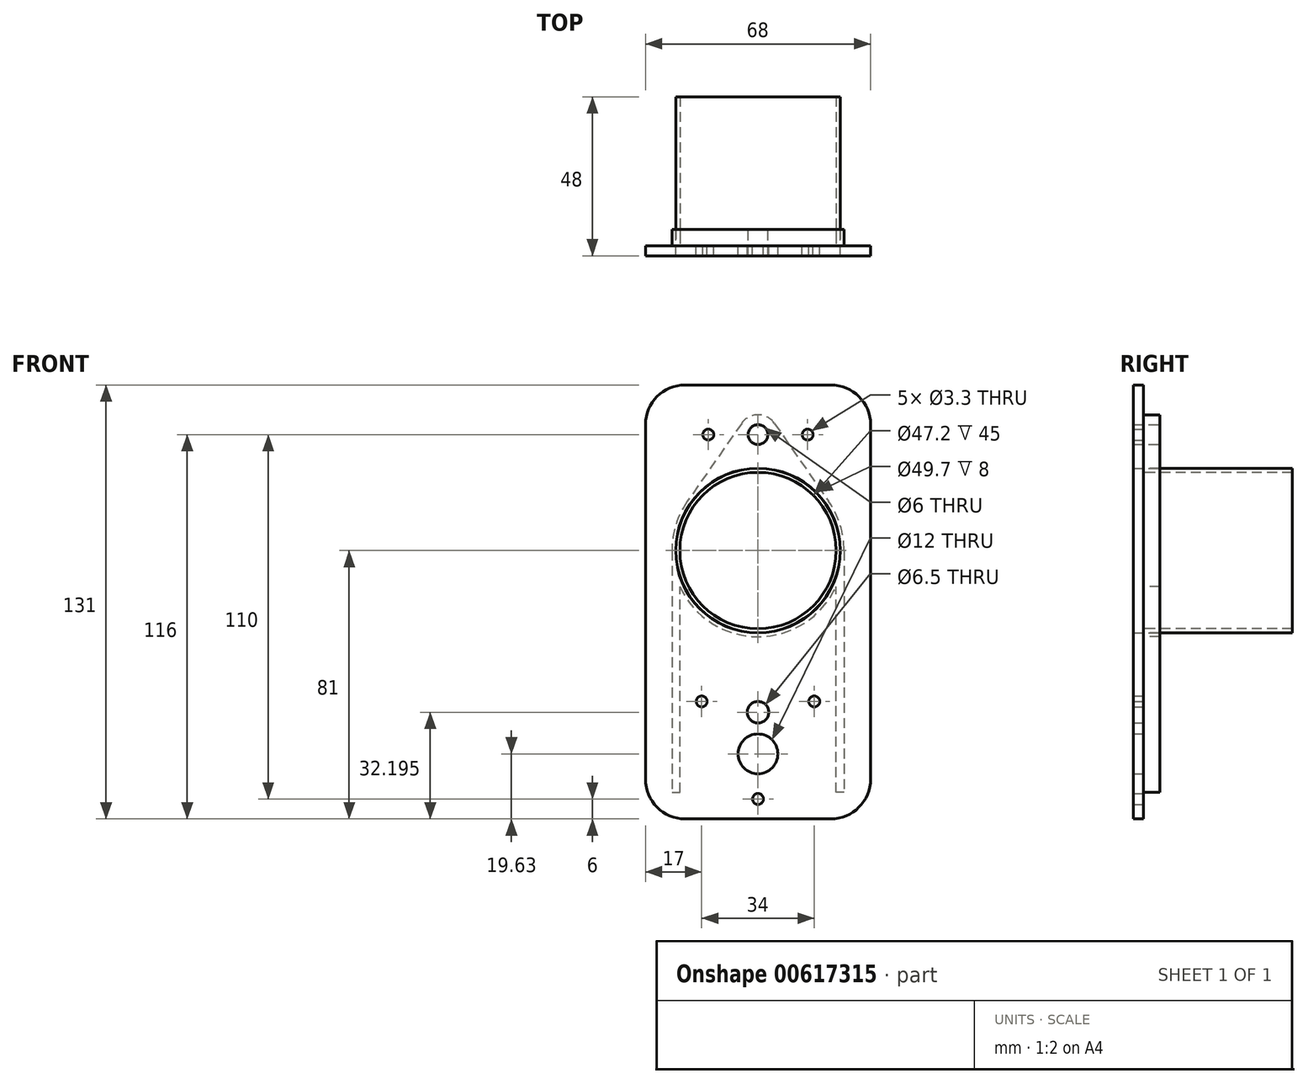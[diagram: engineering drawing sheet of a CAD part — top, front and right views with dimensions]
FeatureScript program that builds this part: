
annotation { "Feature Type Name" : "Feature", "Feature Type Description" : "" }
export const myFeature = defineFeature(function(context is Context, id is Id, definition is map)
    precondition{}
    {
        {
            var Q0;
            Q0=qCreatedBy(makeId("Front.planeOp"),FACE);
            var sketch = newSketch(context, id + "F0", { "sketchPlane" : qUnion([Q0])});
            skLineSegment(sketch, "E0.bottom", {"start": v(34, -65.5) * mm, "end": v(-34, -65.5) * mm});
            skLineSegment(sketch, "E0.top", {"start": v(34, 65.5) * mm, "end": v(-34, 65.5) * mm});
            skLineSegment(sketch, "E0.left", {"start": v(34, -65.5) * mm, "end": v(34, 65.5) * mm});
            skLineSegment(sketch, "E0.right", {"start": v(-34, -65.5) * mm, "end": v(-34, 65.5) * mm});
            skPoint(sketch, "E0.middle", {"position": v(0, 0) * mm});
            skCircle(sketch, "E1", {"center": v(0, 15.5) * mm, "radius": 24.85 * mm});
            skLineSegment(sketch, "E2", {"start": v(0, 15.5) * mm, "end": v(0, -65.5) * mm, "construction": true});
            skPoint(sketch, "E3", {"position": v(0, -59.5) * mm});
            skPoint(sketch, "E4", {"position": v(-17, -30.06) * mm});
            skPoint(sketch, "E5.MirrorP", {"position": v(17, -30.06) * mm});
            skLineSegment(sketch, "E6", {"start": v(-17, -30.06) * mm, "end": v(17, -30.06) * mm, "construction": true});
            skLineSegment(sketch, "E7", {"start": v(0, -59.5) * mm, "end": v(-17, -30.06) * mm, "construction": true});
            skLineSegment(sketch, "E8", {"start": v(17, -30.06) * mm, "end": v(-8.5, -44.78) * mm, "construction": true});
            skCircle(sketch, "E9", {"center": v(0, -39.87) * mm, "radius": 12 * mm, "construction": true});
            skCircle(sketch, "E10", {"center": v(0, 50.5) * mm, "radius": 3 * mm});
            skCircle(sketch, "E11", {"center": v(0, -45.87) * mm, "radius": 6 * mm});
            skCircle(sketch, "E12", {"center": v(0, -33.3) * mm, "radius": 3.25 * mm});
            skPoint(sketch, "E13", {"position": v(15, 50.5) * mm});
            skPoint(sketch, "E14.MirrorP", {"position": v(-15, 50.5) * mm});
            skSolve(sketch);
        }
        {
            var Q0;
            Q0 = qSketchRegion(id + "F0", true);
            extrude(context, id + "F1", {"entities" : qUnion([Q0]), "depth" : 3 * mm, "offsetDistance" : 25 * mm});
        }
        {
            var Q0;
            Q0=makeQuery(id+"F1.opExtrude","CAP_FACE",FACE,{"disambiguationData":[OSD([sQuery(id+"F0.wireOp",EDGE,"E0.bottom"),sQuery(id+"F0.wireOp",EDGE,"E0.top"),sQuery(id+"F0.wireOp",EDGE,"E0.left"),sQuery(id+"F0.wireOp",EDGE,"E0.right"),sQuery(id+"F0.wireOp",EDGE,"E1"),sQuery(id+"F0.wireOp",EDGE,"lBdVOncp-TCnz-bJnv-wLVM-4AzIkIplRtc7"),sQuery(id+"F0.wireOp",EDGE,"E10")])],"isStart":true});
            var sketch = newSketch(context, id + "F2", { "sketchPlane" : qUnion([Q0])});
            skCircle(sketch, "E15.0", {"center": v(0, 15.5) * mm, "radius": 24.85 * mm});
            skCircle(sketch, "E16.0", {"center": v(0, 50.5) * mm, "radius": 3 * mm});
            skArc(sketch, "E17", {"start": v(-23.6, 4.59) * mm, "mid": v(0, -10.5) * mm, "end": v(23.6, 4.59) * mm});
            skArc(sketch, "E18.0", {"start": v(4.92, 53.93) * mm, "mid": v(0, 56.5) * mm, "end": v(-4.92, 53.93) * mm});
            skLineSegment(sketch, "E19", {"start": v(-34, -57.5) * mm, "end": v(34, -57.5) * mm, "construction": true});
            skLineSegment(sketch, "E20", {"start": v(4.92, 53.93) * mm, "end": v(21.34, 30.36) * mm});
            skLineSegment(sketch, "E21", {"start": v(0, 15.5) * mm, "end": v(0, -57.5) * mm, "construction": true});
            skLineSegment(sketch, "E22", {"start": v(26, 15.5) * mm, "end": v(26, -57.5) * mm});
            skLineSegment(sketch, "E23", {"start": v(26, -57.5) * mm, "end": v(23.6, -57.5) * mm});
            skLineSegment(sketch, "E24", {"start": v(23.6, -57.5) * mm, "end": v(23.6, 4.59) * mm});
            skLineSegment(sketch, "E25.MirrorCS", {"start": v(-26, 15.5) * mm, "end": v(-26, -57.5) * mm});
            skLineSegment(sketch, "E26.MirrorCS", {"start": v(-23.6, -57.5) * mm, "end": v(-23.6, 4.59) * mm});
            skLineSegment(sketch, "E27.MirrorCS", {"start": v(-26, -57.5) * mm, "end": v(-23.6, -57.5) * mm});
            skArc(sketch, "E28.trimOffspring", {"start": v(26, 15.5) * mm, "mid": v(24.8, 23.29) * mm, "end": v(21.34, 30.36) * mm});
            skLineSegment(sketch, "E29.MirrorCS", {"start": v(-4.92, 53.93) * mm, "end": v(-21.34, 30.36) * mm});
            skArc(sketch, "E30.trimOffspring", {"start": v(-21.34, 30.36) * mm, "mid": v(-24.8, 23.29) * mm, "end": v(-26, 15.5) * mm});
            skSolve(sketch);
        }
        {
            var Q0;
            Q0 = qSketchRegion(id + "F2", true);
            extrude(context, id + "F3", {"entities" : qUnion([Q0]), "operationType" : NewBodyOperationType.ADD, "depth" : 5 * mm, "offsetDistance" : 25 * mm});
        }
        {
            var Q0;
            Q0=sQuery(id+"F0.wireOp",VERTEX,"E14.MirrorP");
            var Q1;
            Q1=sQuery(id+"F0.wireOp",VERTEX,"E13");
            var Q2;
            Q2=sQuery(id+"F0.wireOp",VERTEX,"E6.start");
            var Q3;
            Q3=sQuery(id+"F0.wireOp",VERTEX,"E6.end");
            var Q4;
            Q4=sQuery(id+"F0.wireOp",VERTEX,"E3");
            var Q5;
            Q5=makeQuery(id+"F1.opExtrude","SWEPT_BODY",BODY,{"disambiguationData":[OSD([sQuery(id+"F0.wireOp",EDGE,"E0.bottom"),sQuery(id+"F0.wireOp",EDGE,"E0.top"),sQuery(id+"F0.wireOp",EDGE,"E0.left"),sQuery(id+"F0.wireOp",EDGE,"E0.right"),sQuery(id+"F0.wireOp",EDGE,"E1"),sQuery(id+"F0.wireOp",EDGE,"E10"),sQuery(id+"F0.wireOp",EDGE,"E11"),sQuery(id+"F0.wireOp",EDGE,"E12")])]});
            hole(context, id + "F4", {"style" : HoleStyle.SIMPLE, "endStyle" : HoleEndStyle.THROUGH, "oppositeDirection" : true, "holeDiameter" : 3.3 * mm, "majorDiameter" : 5 * mm, "isTappedThrough" : true, "tappedDepth" : 7 * mm, "tapClearance" : 6, "startFromSketch" : true, "locations" : qUnion([Q0, Q1, Q2, Q3, Q4]), "scope" : qUnion([Q5])});
        }
        {
            var Q0;
            Q0=makeQuery(id+"F1.opExtrude","SWEPT_EDGE",EDGE,{"disambiguationData":[OSD([sQuery(id+"F0.wireOp",EDGE,"E0.top"),sQuery(id+"F0.wireOp",EDGE,"E0.right")])]});
            var Q1;
            Q1=makeQuery(id+"F1.opExtrude","SWEPT_EDGE",EDGE,{"disambiguationData":[OSD([sQuery(id+"F0.wireOp",EDGE,"E0.top"),sQuery(id+"F0.wireOp",EDGE,"E0.left")])]});
            var Q2;
            Q2=makeQuery(id+"F1.opExtrude","SWEPT_EDGE",EDGE,{"disambiguationData":[OSD([sQuery(id+"F0.wireOp",EDGE,"E0.bottom"),sQuery(id+"F0.wireOp",EDGE,"E0.right")])]});
            var Q3;
            Q3=makeQuery(id+"F1.opExtrude","SWEPT_EDGE",EDGE,{"disambiguationData":[OSD([sQuery(id+"F0.wireOp",EDGE,"E0.bottom"),sQuery(id+"F0.wireOp",EDGE,"E0.left")])]});
            fillet(context, id + "F5", {"entities" : qUnion([Q0, Q1, Q2, Q3]), "radius" : 12 * mm, "tangentPropagation" : true, "allowEdgeOverflow" : false});
        }
        {
            var Q0;
            Q0=qCreatedBy(makeId("Front.planeOp"),FACE);
            var sketch = newSketch(context, id + "F6", { "sketchPlane" : qUnion([Q0])});
            skCircle(sketch, "E31", {"center": v(0, 15.5) * mm, "radius": 23.6 * mm});
            skCircle(sketch, "E32.0", {"center": v(0, 15.5) * mm, "radius": 24.8 * mm});
            skSolve(sketch);
        }
        {
            var Q0;
            Q0 = qSketchRegion(id + "F6", true);
            extrude(context, id + "F7", {"entities" : qUnion([Q0]), "oppositeDirection" : true, "depth" : 45 * mm, "offsetDistance" : 25 * mm});
        }
    });
